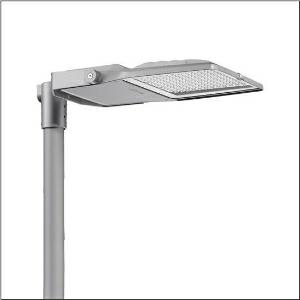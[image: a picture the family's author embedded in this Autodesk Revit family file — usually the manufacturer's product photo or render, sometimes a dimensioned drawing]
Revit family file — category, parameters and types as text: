
# Revit family: floodlight_fl_21_iq_midi___pl64_5xa7782f4e3a_0b41
name_source: partatom
category: Lighting Fixtures
units: mm (PartAtom-declared; Revit-internal decimal feet)

## family parameters
Cut with Voids When Loaded = No
Host = Face
Light Source = No
Part Type = Normal
Room Calculation Point = No
Round Connector Dimension = Use Diameter
Shared = No

## types (1)
- --- (1 x LED, 36050 lm, 270.2 W, 4000K)
    Apparent Load = 270 VA
    CIE Flux Codes = 28 80 98 100 100
    Color Rendering = 70
    Color Temperature = 4000K
    Default Elevation = 1800 mm
    Description = Floodlight FL 21 iQ midi, floodlight, primary light control with lens, of PMMA, primary optical cover: protective disc, of toughened safety glass, transparent, light distribution: PL64, light emission: direct distribution, installation type: surface-mounted, LED, High Power LED, rated luminous flux: 36.050lm, luminous efficacy: 133lm/W, light colour: 740, colour temperature: 4000K, control gear: iQ Street-Remote/DALI, control: optimised constant luminous flux control (CLO 2.0), Desk-Remote (wireless, voltage-free reading and setting of iQ features in the workshop via application-optimized NFC function/RFID function), Smart-Wire, Night-Set, Temp-Guard, Auto-Match, Street-Remote, with terminal, 6-pole, mains connection: 220..240V, AC, 50/60Hz, start of lifetime: 270W, end of service life: 287W, reduction: 118W, luminaire housing, of diecast aluminium, powder-coated, Siteco® metallic grey (DB 702S), corrosivity category C5 mid according to DIN EN ISO 12944, suitable for swimming pools, chlorine-resistant, sealing non-destructively replaceable, please order mast flange separately, mast bracket, of steel, galvanised, powder-coated, Siteco® metallic grey (DB 702S), protection rating (complete): IP66, insulation class (complete): insulation class II (safety insulation), certification: CE, ENEC, VDE, protection symbol: D, impact resistance: IK08, permissible operating ambient temperature: -40..+40°C, permissible operating ambient temperature for outdoor applications: -40..+50°C, standard: DIN EN 12944, LABS conformity tested according to VDMA 24364:2018-05, packaging unit: 1 piece

Light Distribution: PL64
    Height = 76 mm
    Lamp = 1 x LED
    Lamp Light Flux = 36050 lm
    Lamp Power = 270.2 W
    Lamp count = 1
    Length = 657 mm
    Luminous efficacy = 133 lm/W
    Manufacturer = Siteco
    ModVariant = No
    Model = 5XA7782F4E3A
    Number of Poles = 1
    OnlyDefault = Yes
    Power Factor = 1
    Product Name = Floodlight FL 21 iQ midi | PL64
    Product group = floodlight | pylon annexe
    ProductGroupID = 6200
    Protection Class = Protection class II
    Protection Degree = IP 66
    RLX_Detail_Level = 1
    RLX_Emergency_Light_Flux = 0 lm
    RLX_Emergency_Type = 0
    RLX_Emergency_Type_DB = No
    RlxData = <blob elided: 153929 chars, md5=79596b2c>
    Socket = socket
    Standby Power = 0 W
    System Light Flux = 36050 lm
    System Power = 270 W
    Type Comments = factory setting: luminous flux: 100 % | dim-lin: 254 | 620 mA
    Type Image = l_1007123.jpg
    URL = http://relux.com
    VarID = @adj_106564
    Voltage = 0 V
    Weight = 0.00 kg
    Width = 442 mm

## geometry (parser evidence)
native form markers: Blend x4, Sweep x14
no freeform markers — native parametric forms only
